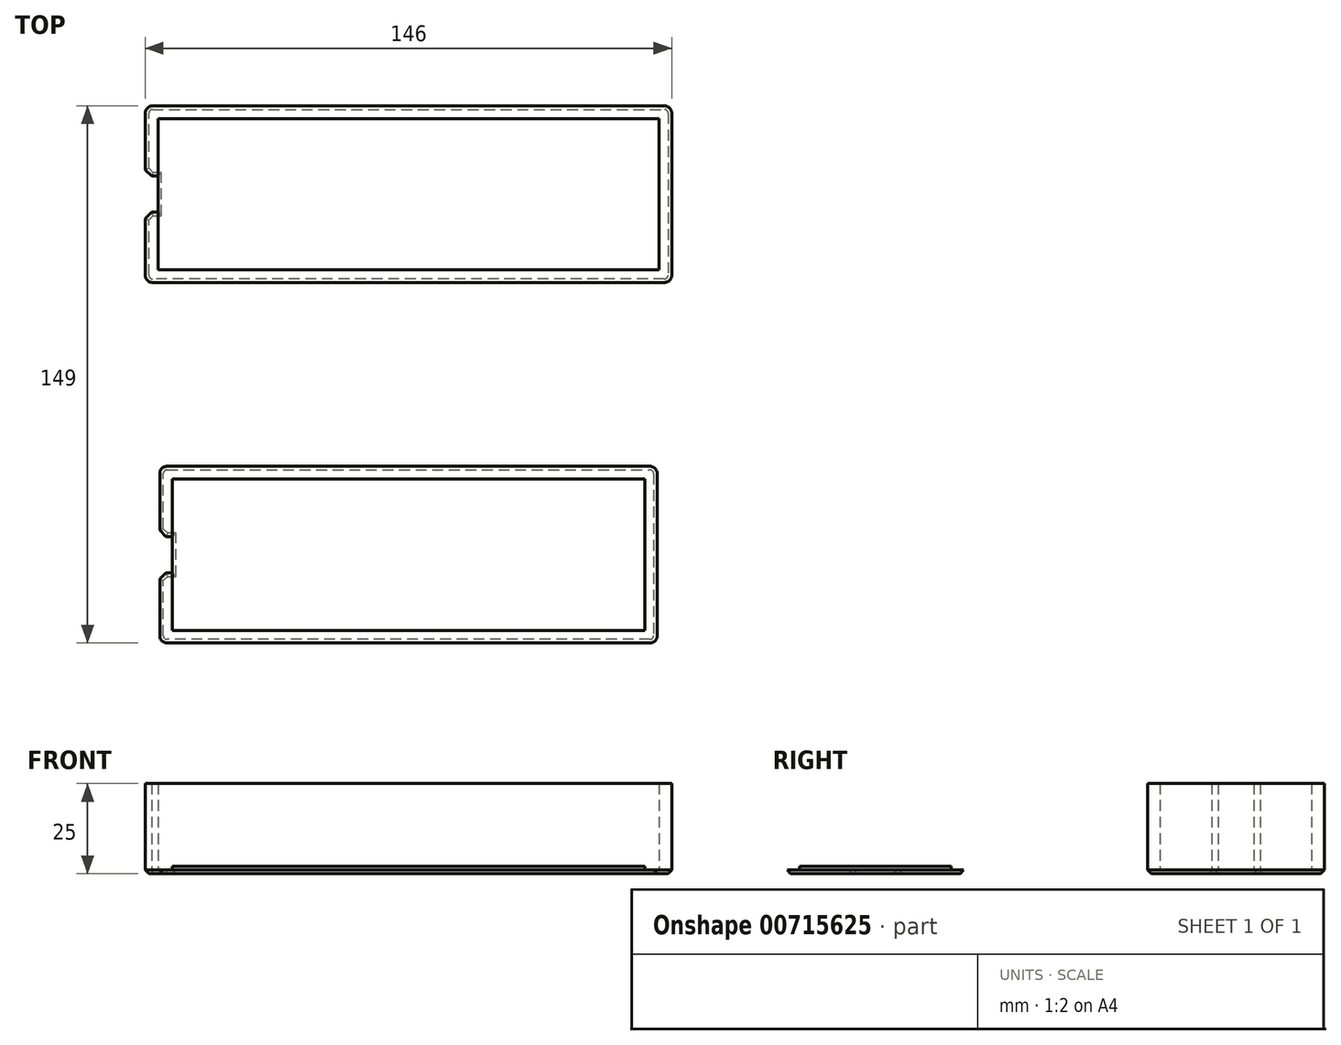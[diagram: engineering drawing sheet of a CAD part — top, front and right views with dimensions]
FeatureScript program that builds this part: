
annotation { "Feature Type Name" : "Feature", "Feature Type Description" : "" }
export const myFeature = defineFeature(function(context is Context, id is Id, definition is map)
    precondition{}
    {
        {
            var Q0;
            Q0=qCreatedBy(makeId("Top.planeOp"),FACE);
            var sketch = newSketch(context, id + "F0", { "sketchPlane" : qUnion([Q0])});
            skLineSegment(sketch, "E0.bottom", {"start": v(-69.5, -21) * mm, "end": v(69.5, -21) * mm});
            skLineSegment(sketch, "E0.top", {"start": v(-69.5, 21) * mm, "end": v(69.5, 21) * mm});
            skLineSegment(sketch, "E0.left", {"start": v(-69.5, -21) * mm, "end": v(-69.5, 21) * mm});
            skLineSegment(sketch, "E0.right", {"start": v(69.5, -21) * mm, "end": v(69.5, 21) * mm});
            skPoint(sketch, "E0.middle", {"position": v(0, 0) * mm});
            skLineSegment(sketch, "E1.0", {"start": v(-71, -24.5) * mm, "end": v(71, -24.5) * mm});
            skLineSegment(sketch, "E1.1", {"start": v(-73, -22.5) * mm, "end": v(-73, -6.75) * mm});
            skLineSegment(sketch, "E1.2", {"start": v(-71, 24.5) * mm, "end": v(71, 24.5) * mm});
            skLineSegment(sketch, "E1.3", {"start": v(73, -22.5) * mm, "end": v(73, 22.5) * mm});
            skPoint(sketch, "E2.visualSharp", {"position": v(73, -24.5) * mm});
            skArc(sketch, "E2.filletArc", {"start": v(71, -24.5) * mm, "mid": v(72.41, -23.91) * mm, "end": v(73, -22.5) * mm});
            skPoint(sketch, "E3.visualSharp", {"position": v(73, 24.5) * mm});
            skArc(sketch, "E3.filletArc", {"start": v(73, 22.5) * mm, "mid": v(72.41, 23.91) * mm, "end": v(71, 24.5) * mm});
            skPoint(sketch, "E4.visualSharp", {"position": v(-73, 24.5) * mm});
            skArc(sketch, "E4.filletArc", {"start": v(-71, 24.5) * mm, "mid": v(-72.41, 23.91) * mm, "end": v(-73, 22.5) * mm});
            skPoint(sketch, "E5.visualSharp", {"position": v(-73, -24.5) * mm});
            skArc(sketch, "E5.filletArc", {"start": v(-73, -22.5) * mm, "mid": v(-72.41, -23.91) * mm, "end": v(-71, -24.5) * mm});
            skLineSegment(sketch, "E6", {"start": v(-69.5, 0) * mm, "end": v(-69.5, 5) * mm, "construction": true});
            skLineSegment(sketch, "E7", {"start": v(-69.5, 5) * mm, "end": v(-71.25, 5) * mm});
            skLineSegment(sketch, "E8.MirrorCS", {"start": v(-69.5, -5) * mm, "end": v(-71.25, -5) * mm});
            skLineSegment(sketch, "E9.trimOffspring", {"start": v(-73, 6.75) * mm, "end": v(-73, 22.5) * mm});
            skLineSegment(sketch, "E10", {"start": v(-71.25, 5) * mm, "end": v(-73, 6.75) * mm});
            skLineSegment(sketch, "E11.MirrorCS", {"start": v(-71.25, -5) * mm, "end": v(-73, -6.75) * mm});
            skPoint(sketch, "E12.orphan", {"position": v(-73, 5) * mm});
            skPoint(sketch, "E13.orphan", {"position": v(-73, -5) * mm});
            skLineSegment(sketch, "E14", {"start": v(0, 0) * mm, "end": v(0, -100) * mm, "construction": true});
            skLineSegment(sketch, "E15.bottom", {"start": v(-65.5, -121) * mm, "end": v(65.5, -121) * mm});
            skLineSegment(sketch, "E15.top", {"start": v(-65.5, -79) * mm, "end": v(65.5, -79) * mm});
            skLineSegment(sketch, "E15.left", {"start": v(-65.5, -121) * mm, "end": v(-65.5, -79) * mm});
            skLineSegment(sketch, "E15.right", {"start": v(65.5, -121) * mm, "end": v(65.5, -79) * mm});
            skPoint(sketch, "E15.middle", {"position": v(0, -100) * mm});
            skLineSegment(sketch, "E16.0", {"start": v(-67, -124.5) * mm, "end": v(67, -124.5) * mm});
            skLineSegment(sketch, "E16.1", {"start": v(-69, -122.5) * mm, "end": v(-69, -106.75) * mm});
            skLineSegment(sketch, "E16.2", {"start": v(-67, -75.5) * mm, "end": v(67, -75.5) * mm});
            skLineSegment(sketch, "E16.3", {"start": v(69, -122.5) * mm, "end": v(69, -77.5) * mm});
            skPoint(sketch, "E17.visualSharp", {"position": v(-69, -75.5) * mm});
            skArc(sketch, "E17.filletArc", {"start": v(-67, -75.5) * mm, "mid": v(-68.41, -76.09) * mm, "end": v(-69, -77.5) * mm});
            skPoint(sketch, "E18.visualSharp", {"position": v(69, -75.5) * mm});
            skArc(sketch, "E18.filletArc", {"start": v(69, -77.5) * mm, "mid": v(68.41, -76.09) * mm, "end": v(67, -75.5) * mm});
            skPoint(sketch, "E19.visualSharp", {"position": v(69, -124.5) * mm});
            skArc(sketch, "E19.filletArc", {"start": v(67, -124.5) * mm, "mid": v(68.41, -123.91) * mm, "end": v(69, -122.5) * mm});
            skPoint(sketch, "E20.visualSharp", {"position": v(-69, -124.5) * mm});
            skArc(sketch, "E20.filletArc", {"start": v(-69, -122.5) * mm, "mid": v(-68.41, -123.91) * mm, "end": v(-67, -124.5) * mm});
            skLineSegment(sketch, "E21", {"start": v(-65.5, -100) * mm, "end": v(-69, -100) * mm, "construction": true});
            skLineSegment(sketch, "E22", {"start": v(-65.5, -100) * mm, "end": v(-65.5, -95) * mm, "construction": true});
            skLineSegment(sketch, "E23", {"start": v(-65.5, -95) * mm, "end": v(-67.25, -95) * mm});
            skLineSegment(sketch, "E24", {"start": v(-67.25, -95) * mm, "end": v(-69, -93.25) * mm});
            skLineSegment(sketch, "E25.MirrorCS", {"start": v(-65.5, -105) * mm, "end": v(-67.25, -105) * mm});
            skLineSegment(sketch, "E26.MirrorCS", {"start": v(-67.25, -105) * mm, "end": v(-69, -106.75) * mm});
            skPoint(sketch, "E27.orphan", {"position": v(-69, -95) * mm});
            skLineSegment(sketch, "E28.trimOffspring", {"start": v(-69, -93.25) * mm, "end": v(-69, -77.5) * mm});
            skPoint(sketch, "E29.orphan", {"position": v(-69, -105) * mm});
            skSolve(sketch);
        }
        {
            var Q0;
            {var subQ3=sQuery(id+"F0.wireOp",EDGE,"E0.bottom");Q0=makeQuery(id+"F0.imprint","IMPRINT",FACE,{"disambiguationData":[TD([[makeQuery(id+"F0.imprint","IMPRINT",EDGE,{"derivedFrom":subQ3}),1.0]])]});}
            extrude(context, id + "F1", {"entities" : qUnion([Q0]), "depth" : 1 * mm, "offsetDistance" : 25 * mm});
        }
        {
            var Q0;
            {var subQ0=sQuery(id+"F0.wireOp",EDGE,"E0.bottom");Q0=makeQuery(id+"F0.imprint","IMPRINT",FACE,{"disambiguationData":[TD([[makeQuery(id+"F0.imprint","IMPRINT",EDGE,{"derivedFrom":subQ0}),-1.0]])]});}
            extrude(context, id + "F2", {"entities" : qUnion([Q0]), "operationType" : NewBodyOperationType.ADD, "depth" : 25 * mm, "offsetDistance" : 25 * mm});
        }
        {
            var Q0;
            Q0=makeQuery(id+"F0.imprint","IMPRINT",FACE,{"disambiguationData":[TD([[makeQuery(id+"F0.imprint","IMPRINT",EDGE,{"derivedFrom":sQuery(id+"F0.wireOp",EDGE,"E15.bottom")}),-1.0]])]});
            extrude(context, id + "F3", {"entities" : qUnion([Q0]), "depth" : 1 * mm, "offsetDistance" : 25 * mm});
        }
        {
            var Q0;
            Q0=makeQuery(id+"F0.imprint","IMPRINT",FACE,{"disambiguationData":[TD([[makeQuery(id+"F0.imprint","IMPRINT",EDGE,{"derivedFrom":sQuery(id+"F0.wireOp",EDGE,"E15.bottom")}),1.0]])]});
            extrude(context, id + "F4", {"entities" : qUnion([Q0]), "operationType" : NewBodyOperationType.ADD, "depth" : 2 * mm, "offsetDistance" : 25 * mm});
        }
        {
            var Q0;
            {var subQ0=sQuery(id+"F0.wireOp",EDGE,"E0.right");var subQ1=sQuery(id+"F0.wireOp",EDGE,"E0.left");var subQ2=sQuery(id+"F0.wireOp",EDGE,"E0.top");var subQ3=sQuery(id+"F0.wireOp",EDGE,"E0.bottom");Q0=makeQuery(id+"F2.boolean.opBoolean","MERGE",FACE,{"derivedFrom":[makeQuery(id+"F1.opExtrude","CAP_FACE",FACE,{"disambiguationData":[OSD([subQ3,subQ2,subQ1,subQ0])],"isStart":true}),makeQuery(id+"F2.opExtrude","CAP_FACE",FACE,{"disambiguationData":[OSD([subQ3,subQ2,subQ1,subQ0,sQuery(id+"F0.wireOp",EDGE,"E1.0"),sQuery(id+"F0.wireOp",EDGE,"E1.1"),sQuery(id+"F0.wireOp",EDGE,"E1.2"),sQuery(id+"F0.wireOp",EDGE,"E1.3"),sQuery(id+"F0.wireOp",EDGE,"E2.filletArc"),sQuery(id+"F0.wireOp",EDGE,"E3.filletArc"),sQuery(id+"F0.wireOp",EDGE,"E4.filletArc"),sQuery(id+"F0.wireOp",EDGE,"E5.filletArc"),sQuery(id+"F0.wireOp",EDGE,"E7"),sQuery(id+"F0.wireOp",EDGE,"E8.MirrorCS"),sQuery(id+"F0.wireOp",EDGE,"E9.trimOffspring"),sQuery(id+"F0.wireOp",EDGE,"E10"),sQuery(id+"F0.wireOp",EDGE,"E11.MirrorCS")])],"isStart":true})]});}
            var Q1;
            Q1=makeQuery(id+"F3.opExtrude","CAP_EDGE",EDGE,{"disambiguationData":[OSD([sQuery(id+"F0.wireOp",EDGE,"E16.0")])],"isStart":true});
            var Q2;
            Q2=makeQuery(id+"F3.opExtrude","CAP_EDGE",EDGE,{"disambiguationData":[OSD([sQuery(id+"F0.wireOp",EDGE,"E26.MirrorCS")])],"isStart":true});
            var Q3;
            Q3=makeQuery(id+"F3.opExtrude","CAP_EDGE",EDGE,{"disambiguationData":[OSD([sQuery(id+"F0.wireOp",EDGE,"E24")])],"isStart":true});
            var Q4;
            Q4=makeQuery(id+"F3.opExtrude","CAP_EDGE",EDGE,{"disambiguationData":[OSD([sQuery(id+"F0.wireOp",EDGE,"E23")])],"isStart":true});
            var Q5;
            Q5=makeQuery(id+"F3.opExtrude","CAP_EDGE",EDGE,{"disambiguationData":[OSD([sQuery(id+"F0.wireOp",EDGE,"E25.MirrorCS")])],"isStart":true});
            var Q6;
            Q6=makeQuery(id+"F4.opExtrude","CAP_EDGE",EDGE,{"disambiguationData":[OSD([sQuery(id+"F0.wireOp",EDGE,"E15.left")])],"isStart":true});
            chamfer(context, id + "F5", {"entities" : qUnion([Q0, Q1, Q2, Q3, Q4, Q5, Q6]), "width" : 1 * mm, "tangentPropagation" : true});
        }
    });
